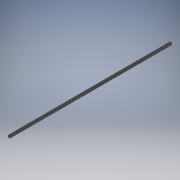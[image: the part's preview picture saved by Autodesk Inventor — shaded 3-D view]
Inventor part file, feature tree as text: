
AUTODESK INVENTOR PART (.ipt)
format: ipt  version: 2018 (Build 220112000, 112)  size: 689,152 bytes
history: native  units: in
note: dims shown in document units (in); Inventor stores cm internally (conversion verified against a paired STEP export)
features: projected_geometry x4, extrude x2, sketch x2, move_body x2, direct_edit x1, other x1
ambient origin geometry x8: Origin, YZ Plane, XZ Plane, XY Plane, X Axis, Y Axis, Z Axis, Center Point
bodies: Solid1 (feature_tree)
feature tree (12):
  direct_edit  "Direct Edit1"
  extrude  "Extrusion1"  Depth=0.813in
  extrude  "Extrusion2"  Depth=0.855in
  sketch  "Sketch1"  dims[d0=0.0in d1=0.0in d2=122.0472in d3=0.813in]
  projected_geometry  "Projected Loop1"
  projected_geometry  "Projected Loop2"
  projected_geometry  "Projected Loop3"
  sketch  "Sketch2"  dims[d4=0.855in d5=0.855in d6=0.813in d7=0.66in d8=0.0in d9=0.0in d10=0.0in d11=123.0in d12=0.3125in d13=18.0in d14=18.0in d15=61.5in d16=0.0in d17=0.0in]
  projected_geometry  "Projected Loop4"
  other  "8020-1515-LS-1515-LS X 145_1_1:1"
  move_body  "Move1"
  move_body  "Move2"
